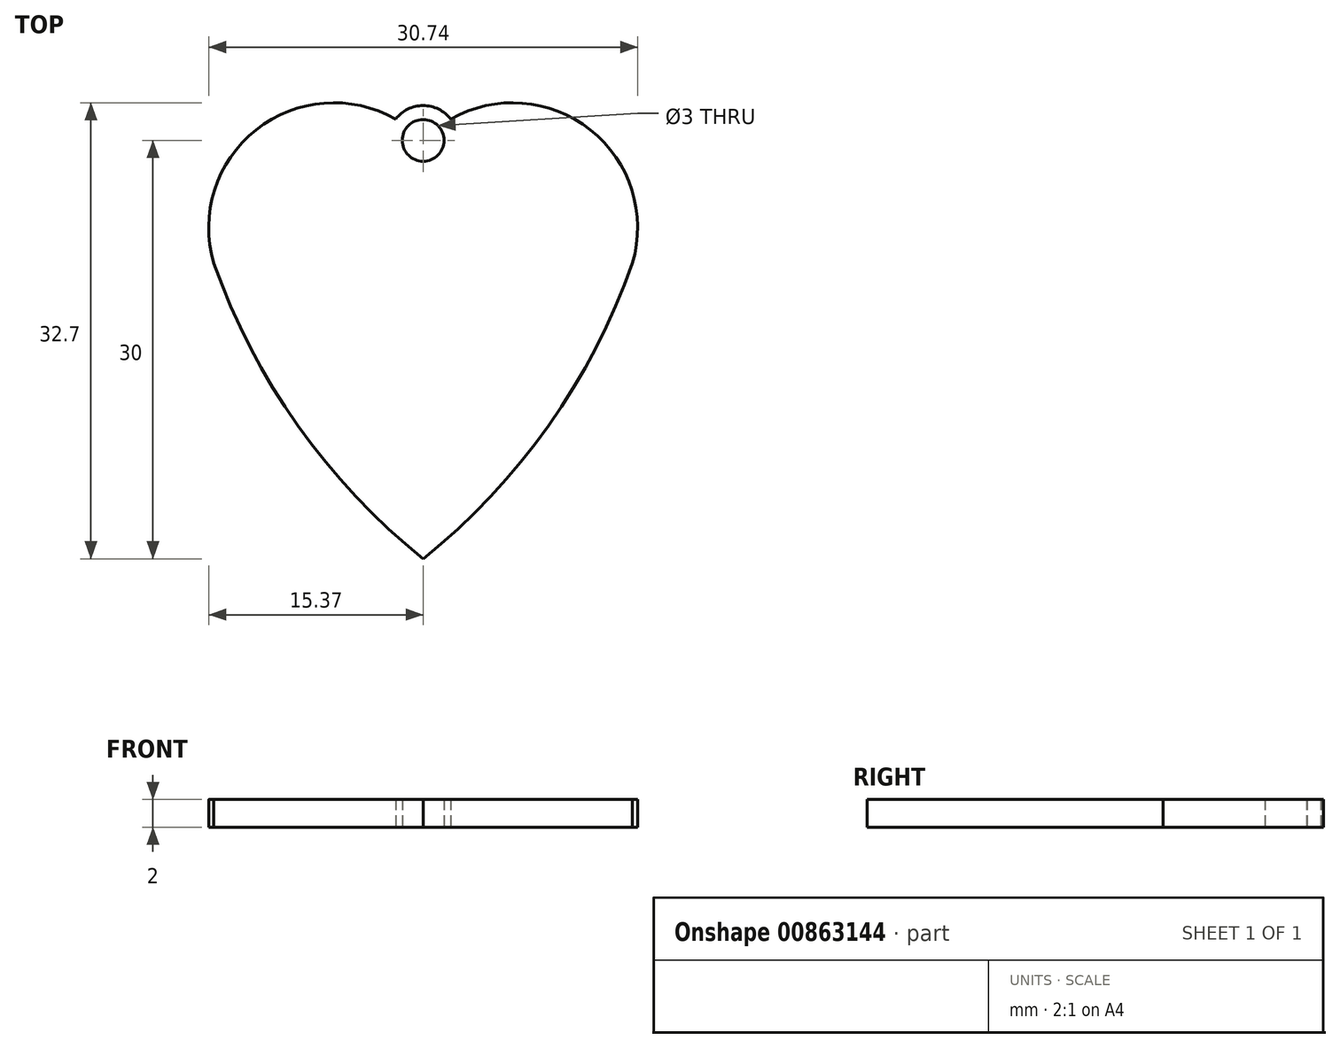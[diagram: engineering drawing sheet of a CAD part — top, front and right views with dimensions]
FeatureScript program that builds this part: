
annotation { "Feature Type Name" : "Feature", "Feature Type Description" : "" }
export const myFeature = defineFeature(function(context is Context, id is Id, definition is map)
    precondition{}
    {
        {
            var Q0;
            Q0=qCreatedBy(makeId("Top.planeOp"),FACE);
            var sketch = newSketch(context, id + "F0", { "sketchPlane" : qUnion([Q0])});
            skPoint(sketch, "E0.middle", {"position": v(0, 0) * mm});
            skArc(sketch, "E1", {"start": v(-15, 6.2) * mm, "mid": v(-8.98, -5.45) * mm, "end": v(0, -15) * mm});
            skArc(sketch, "E2.MirrorCS", {"start": v(15, 6.2) * mm, "mid": v(8.98, -5.45) * mm, "end": v(0, -15) * mm});
            skCircle(sketch, "E3", {"center": v(0, 15) * mm, "radius": 1.5 * mm});
            skArc(sketch, "E4", {"start": v(1.98, 16.53) * mm, "mid": v(0, 17.5) * mm, "end": v(-1.98, 16.53) * mm});
            skArc(sketch, "E5.trimOffspring", {"start": v(-1.98, 16.53) * mm, "mid": v(-11.98, 15.76) * mm, "end": v(-15, 6.2) * mm});
            skArc(sketch, "E6.trimOffspring", {"start": v(1.98, 16.53) * mm, "mid": v(11.98, 15.76) * mm, "end": v(15, 6.2) * mm});
            skSolve(sketch);
        }
        {
            var Q0;
            Q0 = qSketchRegion(id + "F0", true);
            extrude(context, id + "F1", {"entities" : qUnion([Q0]), "depth" : 2 * mm, "offsetDistance" : 25 * mm});
        }
    });
